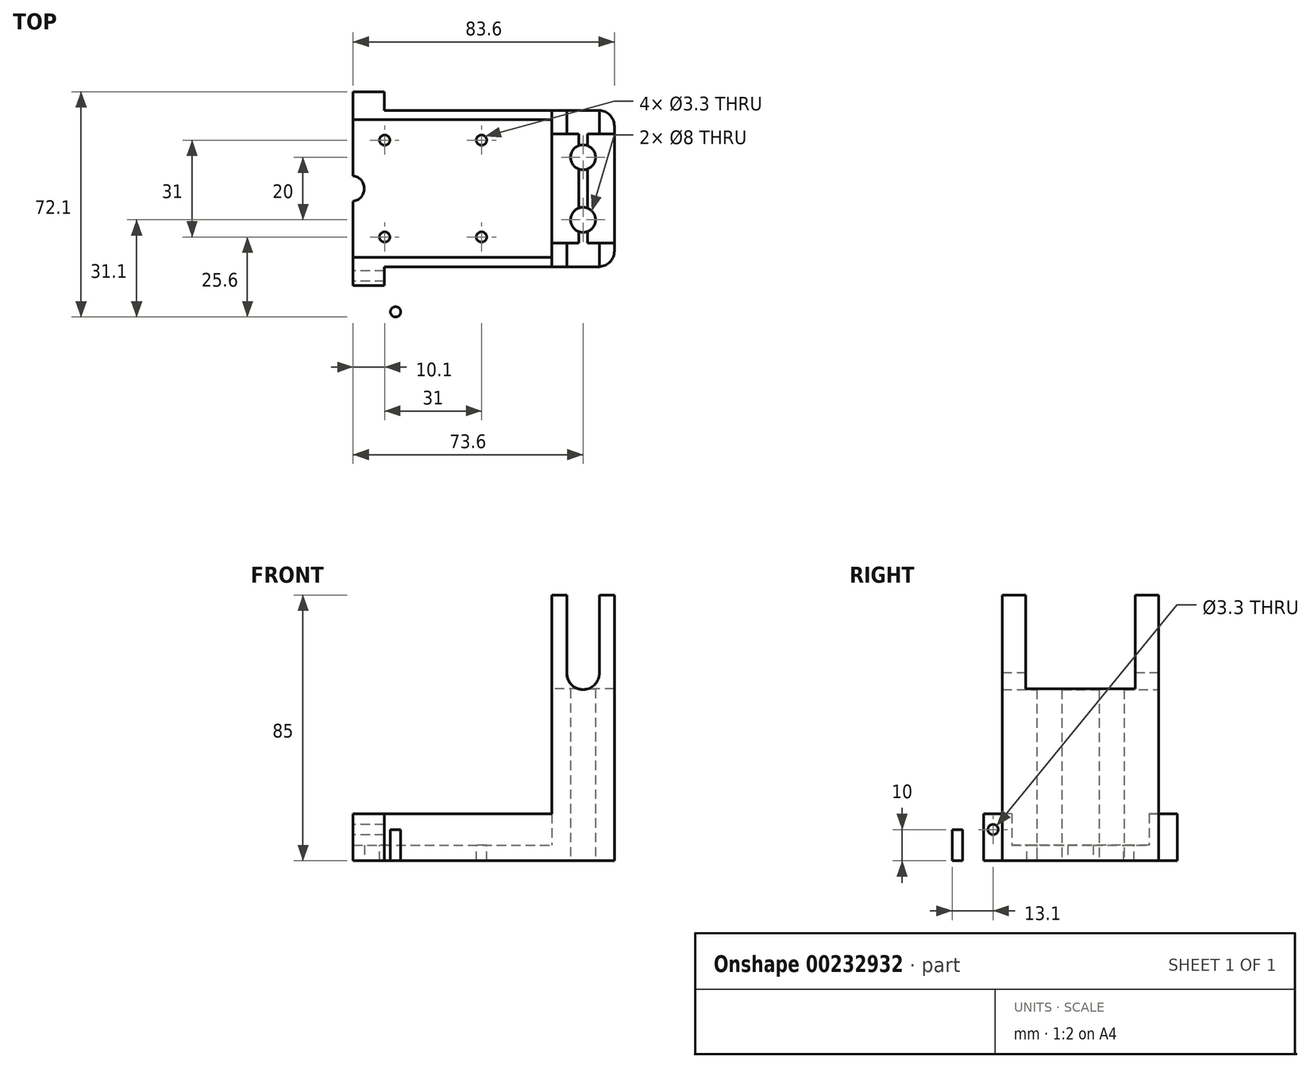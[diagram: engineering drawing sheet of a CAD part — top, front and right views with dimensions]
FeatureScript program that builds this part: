
annotation { "Feature Type Name" : "Feature", "Feature Type Description" : "" }
export const myFeature = defineFeature(function(context is Context, id is Id, definition is map)
    precondition{}
    {
        {
            var Q0;
            Q0=qCreatedBy(makeId("Top.planeOp"),FACE);
            var sketch = newSketch(context, id + "F0", { "sketchPlane" : qUnion([Q0])});
            skLineSegment(sketch, "E0.bottom", {"start": v(0, 0) * mm, "end": v(80, 0) * mm});
            skLineSegment(sketch, "E0.top", {"start": v(0, 50) * mm, "end": v(80, 50) * mm});
            skLineSegment(sketch, "E0.left", {"start": v(0, 0) * mm, "end": v(0, 50) * mm});
            skLineSegment(sketch, "E0.right", {"start": v(80, 0) * mm, "end": v(80, 50) * mm});
            skSolve(sketch);
        }
        {
            var Q0;
            Q0=makeQuery(id+"F0.imprint","IMPRINT",FACE,{"disambiguationData":[TD([[makeQuery(id+"F0.imprint","IMPRINT",EDGE,{"derivedFrom":sQuery(id+"F0.wireOp",EDGE,"E0.bottom")}),1.0]])]});
            extrude(context, id + "F1", {"entities" : qUnion([Q0]), "depth" : 5 * mm});
        }
        {
            var Q0;
            Q0=makeQuery(id+"F1.opExtrude","CAP_FACE",FACE,{"disambiguationData":[OSD([sQuery(id+"F0.wireOp",EDGE,"E0.bottom"),sQuery(id+"F0.wireOp",EDGE,"E0.top"),sQuery(id+"F0.wireOp",EDGE,"E0.left"),sQuery(id+"F0.wireOp",EDGE,"E0.right")])],"isStart":false});
            var sketch = newSketch(context, id + "F2", { "sketchPlane" : qUnion([Q0])});
            skLineSegment(sketch, "E1.0", {"start": v(3, 47) * mm, "end": v(77, 47) * mm});
            skLineSegment(sketch, "E1.2", {"start": v(3, 3) * mm, "end": v(77, 3) * mm});
            skLineSegment(sketch, "E1.3", {"start": v(77, 3) * mm, "end": v(77, 47) * mm});
            skPoint(sketch, "E2", {"position": v(60, 50) * mm});
            skLineSegment(sketch, "E3", {"start": v(60, 50) * mm, "end": v(60, 0) * mm});
            skLineSegment(sketch, "E4", {"start": v(3, 47) * mm, "end": v(0, 47) * mm});
            skLineSegment(sketch, "E5", {"start": v(3, 3) * mm, "end": v(0, 3) * mm});
            skPoint(sketch, "E6", {"position": v(6.5, 40.5) * mm});
            skPoint(sketch, "E7", {"position": v(6.5, 9.5) * mm});
            skPoint(sketch, "E8", {"position": v(37.5, 40.5) * mm});
            skPoint(sketch, "E9", {"position": v(37.5, 9.5) * mm});
            skSolve(sketch);
        }
        {
            var Q0;
            {var subQ5=sQuery(id+"F2.wireOp",EDGE,"E4");Q0=makeQuery(id+"F2.imprint","IMPRINT",FACE,{"disambiguationData":[TD([[makeQuery(id+"F2.imprint","IMPRINT",EDGE,{"derivedFrom":subQ5}),-1.0]])]});}
            var Q1;
            {var subQ5=sQuery(id+"F2.wireOp",EDGE,"E5");Q1=makeQuery(id+"F2.imprint","IMPRINT",FACE,{"disambiguationData":[TD([[makeQuery(id+"F2.imprint","IMPRINT",EDGE,{"derivedFrom":subQ5}),1.0]])]});}
            extrude(context, id + "F3", {"entities" : qUnion([Q0, Q1]), "operationType" : NewBodyOperationType.ADD, "depth" : 10 * mm});
        }
        {
            var Q0;
            {var subQ0=sQuery(id+"F2.wireOp",EDGE,"E1.3");Q0=makeQuery(id+"F2.imprint","IMPRINT",FACE,{"disambiguationData":[TD([[makeQuery(id+"F2.imprint","IMPRINT",EDGE,{"derivedFrom":subQ0}),1.0]])]});}
            var Q1;
            {var subQ0=sQuery(id+"F2.wireOp",EDGE,"E1.3");Q1=makeQuery(id+"F2.imprint","IMPRINT",FACE,{"disambiguationData":[TD([[makeQuery(id+"F2.imprint","IMPRINT",EDGE,{"derivedFrom":subQ0}),-1.0]])]});}
            extrude(context, id + "F4", {"entities" : qUnion([Q0, Q1]), "operationType" : NewBodyOperationType.ADD, "depth" : 80 * mm});
        }
        {
            var Q0;
            Q0=sQuery(id+"F2.wireOp",VERTEX,"E8");
            var Q1;
            Q1=sQuery(id+"F2.wireOp",VERTEX,"E9");
            var Q2;
            Q2=sQuery(id+"F2.wireOp",VERTEX,"E7");
            var Q3;
            Q3=sQuery(id+"F2.wireOp",VERTEX,"E6");
            var Q4;
            Q4=makeQuery(id+"F1.opExtrude","SWEPT_BODY",BODY,{"disambiguationData":[OSD([sQuery(id+"F0.wireOp",EDGE,"E0.bottom"),sQuery(id+"F0.wireOp",EDGE,"E0.top"),sQuery(id+"F0.wireOp",EDGE,"E0.left"),sQuery(id+"F0.wireOp",EDGE,"E0.right")])]});
            hole(context, id + "F5", {"style" : HoleStyle.SIMPLE, "endStyle" : HoleEndStyle.THROUGH, "standardTappedOrClearance" : lookupTablePath({ "standard" : "ISO", "fit" : "Normal", "size" : "M3", "type" : "Clearance" }), "standardBlindInLast" : lookupTablePath({ "fit" : "Standard", "standard" : "ISO", "size" : "M3", "type" : "Clearance" }), "holeDiameter" : 3.3 * mm, "tappedDepth" : 12 * mm, "tapClearance" : 3, "locations" : qUnion([Q0, Q1, Q2, Q3]), "scope" : qUnion([Q4])});
        }
        {
            var Q0;
            {var subQ0=sQuery(id+"F0.wireOp",EDGE,"E0.left");var subQ1=makeQuery(id+"F1.opExtrude","CAP_EDGE",EDGE,{"disambiguationData":[OSD([subQ0])],"isStart":false});Q0=makeQuery(id+"F3.boolean.opBoolean","MERGE",FACE,{"derivedFrom":[makeQuery(id+"F1.opExtrude","SWEPT_FACE",FACE,{"disambiguationData":[OSD([subQ0])]}),makeQuery(id+"F3.opExtrude","SWEPT_FACE",FACE,{"disambiguationData":[OSD([subQ0]),TDD([makeQuery(id+"F2.imprint","IMPRINT",EDGE,{"disambiguationData":[TD([[makeQuery(id+"F2.imprint","INTERSECT",VERTEX,{"derivedFrom":[makeQuery(id+"F1.opExtrude","CAP_EDGE",EDGE,{"disambiguationData":[OSD([sQuery(id+"F0.wireOp",EDGE,"E0.bottom")])],"isStart":false}),subQ1]}),-1.0]])],"derivedFrom":subQ1})])]}),makeQuery(id+"F3.opExtrude","SWEPT_FACE",FACE,{"disambiguationData":[OSD([subQ0]),TDD([makeQuery(id+"F2.imprint","IMPRINT",EDGE,{"disambiguationData":[TD([[makeQuery(id+"F2.imprint","INTERSECT",VERTEX,{"derivedFrom":[makeQuery(id+"F1.opExtrude","CAP_EDGE",EDGE,{"disambiguationData":[OSD([sQuery(id+"F0.wireOp",EDGE,"E0.top")])],"isStart":false}),subQ1]}),1.0]])],"derivedFrom":subQ1})])]})]});}
            extrude(context, id + "F6", {"entities" : qUnion([Q0]), "operationType" : NewBodyOperationType.ADD, "depth" : 3.6 * mm});
        }
        {
            var Q0;
            {var subQ0=sQuery(id+"F0.wireOp",EDGE,"E0.left");Q0=makeQuery(id+"F6.boolean.opBoolean","MERGE",FACE,{"derivedFrom":[makeQuery(id+"F1.opExtrude","CAP_FACE",FACE,{"disambiguationData":[OSD([sQuery(id+"F0.wireOp",EDGE,"E0.bottom"),sQuery(id+"F0.wireOp",EDGE,"E0.top"),subQ0,sQuery(id+"F0.wireOp",EDGE,"E0.right")])],"isStart":true}),makeQuery(id+"F6.opExtrude","SWEPT_FACE",FACE,{"disambiguationData":[OSD([subQ0]),TDD([makeQuery(id+"F1.opExtrude","CAP_EDGE",EDGE,{"disambiguationData":[OSD([subQ0])],"isStart":true})])]})]});}
            var sketch = newSketch(context, id + "F7", { "sketchPlane" : qUnion([Q0])});
            skPoint(sketch, "E10", {"position": v(-4.1, -25) * mm});
            skPoint(sketch, "E10.positionSnap0", {"position": v(-3.6, -25) * mm});
            skCircle(sketch, "E11", {"center": v(-4.1, -25) * mm, "radius": 4.1 * mm});
            skLineSegment(sketch, "E12", {"start": v(-4.1, -25) * mm, "end": v(-3.6, -25) * mm});
            skLineSegment(sketch, "E13", {"start": v(-3.6, -25) * mm, "end": v(-3.6, 0) * mm});
            skLineSegment(sketch, "E14", {"start": v(-3.6, -25) * mm, "end": v(-3.6, -50) * mm});
            skLineSegment(sketch, "E15.bottom", {"start": v(-3.6, -50) * mm, "end": v(6.4, -50) * mm});
            skLineSegment(sketch, "E15.top", {"start": v(-3.6, -56) * mm, "end": v(6.4, -56) * mm});
            skLineSegment(sketch, "E15.left", {"start": v(-3.6, -50) * mm, "end": v(-3.6, -56) * mm});
            skLineSegment(sketch, "E15.right", {"start": v(6.4, -50) * mm, "end": v(6.4, -56) * mm});
            skLineSegment(sketch, "E16", {"start": v(-3.6, -25) * mm, "end": v(10.88, -25) * mm, "construction": true});
            skLineSegment(sketch, "E17.MirrorCS", {"start": v(-3.6, 6) * mm, "end": v(6.4, 6) * mm});
            skLineSegment(sketch, "E18.MirrorCS", {"start": v(6.4, 0) * mm, "end": v(6.4, 6) * mm});
            skLineSegment(sketch, "E19.MirrorCS", {"start": v(-3.6, 0) * mm, "end": v(-3.6, 6) * mm});
            skSolve(sketch);
        }
        {
            var Q0;
            {var subQ0=sQuery(id+"F7.wireOp",EDGE,"E13");var subQ1=sQuery(id+"F7.wireOp",EDGE,"E11");var subQ2=makeQuery(id+"F7.imprint","INTERSECT",VERTEX,{"derivedFrom":[subQ1,subQ0]});Q0=makeQuery(id+"F7.imprint","IMPRINT",FACE,{"disambiguationData":[TD([[makeQuery(id+"F7.imprint","IMPRINT",EDGE,{"disambiguationData":[TD([[subQ2,1.0]])],"derivedFrom":subQ1}),1.0]])]});}
            extrude(context, id + "F8", {"entities" : qUnion([Q0]), "operationType" : NewBodyOperationType.REMOVE, "oppositeDirection" : true, "depth" : 25 * mm});
        }
        {
            var Q0;
            Q0=makeQuery(id+"F7.imprint","IMPRINT",FACE,{"disambiguationData":[TD([[makeQuery(id+"F7.imprint","IMPRINT",EDGE,{"derivedFrom":sQuery(id+"F7.wireOp",EDGE,"E17.MirrorCS")}),-1.0]])]});
            var Q1;
            Q1=makeQuery(id+"F7.imprint","IMPRINT",FACE,{"disambiguationData":[TD([[makeQuery(id+"F7.imprint","IMPRINT",EDGE,{"derivedFrom":sQuery(id+"F7.wireOp",EDGE,"E15.bottom")}),-1.0]])]});
            extrude(context, id + "F9", {"entities" : qUnion([Q0, Q1]), "operationType" : NewBodyOperationType.ADD, "oppositeDirection" : true, "depth" : 15 * mm});
        }
        {
            var Q0;
            {var subQ0=sQuery(id+"F0.wireOp",EDGE,"E0.left");var subQ1=sQuery(id+"F0.wireOp",EDGE,"E0.bottom");Q0=makeQuery(id+"F9.boolean.opBoolean","MERGE",FACE,{"derivedFrom":[makeQuery(id+"F8.boolean.opBoolean","SPLIT",FACE,{"disambiguationData":[TD([makeQuery(id+"F1.opExtrude","SWEPT_FACE",FACE,{"disambiguationData":[OSD([subQ1])]})])],"derivedFrom":makeQuery(id+"F6.opExtrude","CAP_FACE",FACE,{"disambiguationData":[OSD([subQ0])],"isStart":false})}),makeQuery(id+"F9.opExtrude","SWEPT_FACE",FACE,{"disambiguationData":[OSD([sQuery(id+"F7.wireOp",EDGE,"E19.MirrorCS")])]})]});}
            var sketch = newSketch(context, id + "F10", { "sketchPlane" : qUnion([Q0])});
            skCircle(sketch, "E20", {"center": v(3, 10) * mm, "radius": 1.65 * mm});
            skPoint(sketch, "E20.centerSnap0", {"position": v(-3, 10) * mm});
            skPoint(sketch, "E21.0", {"position": v(-25, 0) * mm});
            skLineSegment(sketch, "E22", {"start": v(-25, 0) * mm, "end": v(-25, 12.79) * mm, "construction": true});
            skCircle(sketch, "E23.MirrorC", {"center": v(-53, 10) * mm, "radius": 1.65 * mm});
            skSolve(sketch);
        }
        {
            var Q0;
            Q0=makeQuery(id+"F10.imprint","IMPRINT",FACE,{"disambiguationData":[TD([[makeQuery(id+"F10.imprint","IMPRINT",EDGE,{"derivedFrom":sQuery(id+"F10.wireOp",EDGE,"E20")}),1.0]])]});
            var Q1;
            Q1=makeQuery(id+"F10.imprint","IMPRINT",FACE,{"disambiguationData":[TD([[makeQuery(id+"F10.imprint","IMPRINT",EDGE,{"derivedFrom":sQuery(id+"F10.wireOp",EDGE,"E23.MirrorC")}),-1.0]])]});
            extrude(context, id + "F11", {"entities" : qUnion([Q0, Q1]), "operationType" : NewBodyOperationType.REMOVE, "oppositeDirection" : true, "depth" : 25 * mm});
        }
        {
            var Q0;
            Q0=qCreatedBy(makeId("Top.planeOp"),FACE);
            var sketch = newSketch(context, id + "F12", { "sketchPlane" : qUnion([Q0])});
            skLineSegment(sketch, "E24.bottom", {"start": v(0, -11.45) * mm, "end": v(15, -11.45) * mm});
            skLineSegment(sketch, "E24.top", {"start": v(0, -73.45) * mm, "end": v(15, -73.45) * mm});
            skLineSegment(sketch, "E24.left", {"start": v(0, -11.45) * mm, "end": v(0, -73.45) * mm});
            skLineSegment(sketch, "E24.right", {"start": v(15, -11.45) * mm, "end": v(15, -73.45) * mm});
            skPoint(sketch, "E25", {"position": v(15, -20.45) * mm});
            skPoint(sketch, "E26", {"position": v(5, -20.45) * mm});
            skLineSegment(sketch, "E27", {"start": v(0, -42.45) * mm, "end": v(8.49, -42.45) * mm, "construction": true});
            skPoint(sketch, "E27.endSnap0", {"position": v(0, -42.45) * mm});
            skLineSegment(sketch, "E28", {"start": v(5, -20.45) * mm, "end": v(15, -20.45) * mm});
            skLineSegment(sketch, "E29", {"start": v(5, -20.45) * mm, "end": v(5, -42.45) * mm});
            skLineSegment(sketch, "E30.MirrorCS", {"start": v(5, -64.45) * mm, "end": v(5, -42.45) * mm});
            skLineSegment(sketch, "E31.MirrorCS", {"start": v(5, -64.45) * mm, "end": v(15, -64.45) * mm});
            skSolve(sketch);
        }
        {
            var Q0;
            {var subQ1=sQuery(id+"F12.wireOp",EDGE,"E24.bottom");Q0=makeQuery(id+"F12.imprint","IMPRINT",FACE,{"disambiguationData":[TD([[makeQuery(id+"F12.imprint","IMPRINT",EDGE,{"derivedFrom":subQ1}),-1.0]])]});}
            extrude(context, id + "F13", {"entities" : qUnion([Q0]), "depth" : 10 * mm});
        }
        {
            var Q0;
            Q0=makeQuery(id+"F13.opExtrude","SWEPT_FACE",FACE,{"disambiguationData":[OSD([sQuery(id+"F12.wireOp",EDGE,"E29"),sQuery(id+"F12.wireOp",EDGE,"E30.MirrorCS")])]});
            var sketch = newSketch(context, id + "F14", { "sketchPlane" : qUnion([Q0])});
            skPoint(sketch, "E32", {"position": v(-42.45, -0.5) * mm});
            skPoint(sketch, "E32.positionSnap0", {"position": v(-42.45, 0) * mm});
            skCircle(sketch, "E33", {"center": v(-42.45, -0.5) * mm, "radius": 4.1 * mm});
            skSolve(sketch);
        }
        {
            var Q0;
            {var subQ0=sQuery(id+"F14.wireOp",EDGE,"E33");var subQ1=makeQuery(id+"F13.opExtrude","CAP_EDGE",EDGE,{"disambiguationData":[OSD([sQuery(id+"F12.wireOp",EDGE,"E29"),sQuery(id+"F12.wireOp",EDGE,"E30.MirrorCS")])],"isStart":true});var subQ2=makeQuery(id+"F14.imprint","INTERSECT",VERTEX,{"disambiguationData":[OD(0.0)],"derivedFrom":[subQ1,subQ0]});Q0=makeQuery(id+"F14.imprint","IMPRINT",FACE,{"disambiguationData":[TD([[makeQuery(id+"F14.imprint","IMPRINT",EDGE,{"disambiguationData":[TD([[subQ2,-1.0]])],"derivedFrom":subQ0}),1.0]])]});}
            extrude(context, id + "F15", {"entities" : qUnion([Q0]), "operationType" : NewBodyOperationType.REMOVE, "oppositeDirection" : true, "depth" : 25 * mm});
        }
        {
            var Q0;
            Q0=makeQuery(id+"F13.opExtrude","CAP_FACE",FACE,{"disambiguationData":[OSD([sQuery(id+"F12.wireOp",EDGE,"E24.bottom"),sQuery(id+"F12.wireOp",EDGE,"E24.top"),sQuery(id+"F12.wireOp",EDGE,"E24.left"),sQuery(id+"F12.wireOp",EDGE,"E24.right"),sQuery(id+"F12.wireOp",EDGE,"E28"),sQuery(id+"F12.wireOp",EDGE,"E29"),sQuery(id+"F12.wireOp",EDGE,"E30.MirrorCS"),sQuery(id+"F12.wireOp",EDGE,"E31.MirrorCS")])],"isStart":false});
            var sketch = newSketch(context, id + "F16", { "sketchPlane" : qUnion([Q0])});
            skPoint(sketch, "E34", {"position": v(10, -70.45) * mm});
            skLineSegment(sketch, "E35", {"start": v(5, -42.45) * mm, "end": v(11.3, -42.45) * mm, "construction": true});
            skCircle(sketch, "E36", {"center": v(10, -70.45) * mm, "radius": 1.65 * mm});
            skCircle(sketch, "E37.MirrorC", {"center": v(10, -14.45) * mm, "radius": 1.65 * mm});
            skSolve(sketch);
        }
        {
            var Q0;
            Q0=makeQuery(id+"F16.imprint","IMPRINT",FACE,{"disambiguationData":[TD([[makeQuery(id+"F16.imprint","IMPRINT",EDGE,{"derivedFrom":sQuery(id+"F16.wireOp",EDGE,"E37.MirrorC")}),-1.0]])]});
            var Q1;
            Q1=makeQuery(id+"F16.imprint","IMPRINT",FACE,{"disambiguationData":[TD([[makeQuery(id+"F16.imprint","IMPRINT",EDGE,{"derivedFrom":sQuery(id+"F16.wireOp",EDGE,"E36")}),1.0]])]});
            extrude(context, id + "F17", {"entities" : qUnion([Q0, Q1]), "operationType" : NewBodyOperationType.REMOVE, "oppositeDirection" : true, "depth" : 25 * mm});
        }
        {
            var Q0;
            {var subQ0=sQuery(id+"F0.wireOp",EDGE,"E0.top");Q0=makeQuery(id+"F6.boolean.opBoolean","MERGE",FACE,{"derivedFrom":[makeQuery(id+"F4.boolean.opBoolean","MERGE",FACE,{"derivedFrom":[makeQuery(id+"F3.boolean.opBoolean","MERGE",FACE,{"derivedFrom":[makeQuery(id+"F1.opExtrude","SWEPT_FACE",FACE,{"disambiguationData":[OSD([subQ0])]}),makeQuery(id+"F3.opExtrude","SWEPT_FACE",FACE,{"disambiguationData":[OSD([subQ0])]})]}),makeQuery(id+"F4.opExtrude","SWEPT_FACE",FACE,{"disambiguationData":[OSD([subQ0])]})]}),makeQuery(id+"F6.opExtrude","SWEPT_FACE",FACE,{"disambiguationData":[OSD([subQ0,sQuery(id+"F0.wireOp",EDGE,"E0.left")])]})]});}
            var sketch = newSketch(context, id + "F18", { "sketchPlane" : qUnion([Q0])});
            skPoint(sketch, "E38", {"position": v(-70, 60) * mm});
            skPoint(sketch, "E38.positionSnap0", {"position": v(-70, 85) * mm});
            skCircle(sketch, "E39", {"center": v(-70, 60) * mm, "radius": 5.2 * mm});
            skLineSegment(sketch, "E40", {"start": v(-75.2, 60.25) * mm, "end": v(-75.2, 85) * mm});
            skLineSegment(sketch, "E41", {"start": v(-64.8, 60) * mm, "end": v(-64.8, 85) * mm});
            skSolve(sketch);
        }
        {
            var Q0;
            Q0=makeQuery(id+"F4.opExtrude","CAP_FACE",FACE,{"disambiguationData":[OSD([sQuery(id+"F0.wireOp",EDGE,"E0.bottom"),sQuery(id+"F0.wireOp",EDGE,"E0.top"),sQuery(id+"F0.wireOp",EDGE,"E0.right"),sQuery(id+"F2.wireOp",EDGE,"E3")])],"isStart":false});
            var sketch = newSketch(context, id + "F19", { "sketchPlane" : qUnion([Q0])});
            skPoint(sketch, "E42", {"position": v(80, 25) * mm});
            skPoint(sketch, "E43", {"position": v(80, 42.5) * mm});
            skPoint(sketch, "E44", {"position": v(80, 7.5) * mm});
            skLineSegment(sketch, "E45", {"start": v(80, 7.5) * mm, "end": v(60, 7.5) * mm});
            skLineSegment(sketch, "E46", {"start": v(80, 42.5) * mm, "end": v(60, 42.5) * mm});
            skSolve(sketch);
        }
        {
            var Q0;
            {var subQ0=sQuery(id+"F19.wireOp",EDGE,"E45");Q0=makeQuery(id+"F19.imprint","IMPRINT",FACE,{"disambiguationData":[TD([[makeQuery(id+"F19.imprint","IMPRINT",EDGE,{"derivedFrom":subQ0}),-1.0]])]});}
            extrude(context, id + "F20", {"entities" : qUnion([Q0]), "operationType" : NewBodyOperationType.REMOVE, "oppositeDirection" : true, "depth" : 30 * mm});
        }
        {
            var Q0;
            Q0 = qSketchRegion(id + "F18", true);
            var Q1;
            {var subQ0=sQuery(id+"F18.wireOp",EDGE,"E40");Q1=makeQuery(id+"F18.imprint","IMPRINT",FACE,{"disambiguationData":[TD([[makeQuery(id+"F18.imprint","IMPRINT",EDGE,{"derivedFrom":subQ0}),-1.0]])]});}
            extrude(context, id + "F21", {"entities" : qUnion([Q0, Q1]), "operationType" : NewBodyOperationType.REMOVE, "oppositeDirection" : true, "depth" : 80 * mm});
        }
        {
            var Q0;
            {var subQ5=sQuery(id+"F7.wireOp",EDGE,"E15.bottom");Q0=makeQuery(id+"F7.imprint","IMPRINT",FACE,{"disambiguationData":[TD([[makeQuery(id+"F7.imprint","IMPRINT",EDGE,{"derivedFrom":subQ5}),1.0]])]});}
            var sketch = newSketch(context, id + "F22", { "sketchPlane" : qUnion([Q0])});
            skPoint(sketch, "E47.0", {"position": v(80, 0) * mm});
            skPoint(sketch, "E48", {"position": v(70, 0) * mm});
            skPoint(sketch, "E49.0", {"position": v(80, -25) * mm});
            skPoint(sketch, "E50", {"position": v(70, -25) * mm});
            skCircle(sketch, "E51", {"center": v(70, -15) * mm, "radius": 4 * mm});
            skCircle(sketch, "E52", {"center": v(70, -35) * mm, "radius": 4 * mm});
            skSolve(sketch);
        }
        {
            var Q0;
            Q0=makeQuery(id+"F22.imprint","IMPRINT",FACE,{"disambiguationData":[TD([[makeQuery(id+"F22.imprint","IMPRINT",EDGE,{"derivedFrom":sQuery(id+"F22.wireOp",EDGE,"E51")}),1.0]])]});
            var Q1;
            Q1=makeQuery(id+"F22.imprint","IMPRINT",FACE,{"disambiguationData":[TD([[makeQuery(id+"F22.imprint","IMPRINT",EDGE,{"derivedFrom":sQuery(id+"F22.wireOp",EDGE,"E52")}),1.0]])]});
            extrude(context, id + "F23", {"entities" : qUnion([Q0, Q1]), "operationType" : NewBodyOperationType.REMOVE, "oppositeDirection" : true, "depth" : 60 * mm});
        }
        {
            var Q0;
            {var subQ0=sQuery(id+"F0.wireOp",EDGE,"E0.right");var subQ1=sQuery(id+"F0.wireOp",EDGE,"E0.top");Q0=makeQuery(id+"F4.boolean.opBoolean","MERGE",EDGE,{"derivedFrom":[makeQuery(id+"F1.opExtrude","SWEPT_EDGE",EDGE,{"disambiguationData":[OSD([subQ1,subQ0])]}),makeQuery(id+"F4.opExtrude","SWEPT_EDGE",EDGE,{"disambiguationData":[OSD([subQ1,subQ0])]})]});}
            var Q1;
            {var subQ0=sQuery(id+"F0.wireOp",EDGE,"E0.right");var subQ1=sQuery(id+"F0.wireOp",EDGE,"E0.bottom");Q1=makeQuery(id+"F4.boolean.opBoolean","MERGE",EDGE,{"derivedFrom":[makeQuery(id+"F1.opExtrude","SWEPT_EDGE",EDGE,{"disambiguationData":[OSD([subQ1,subQ0])]}),makeQuery(id+"F4.opExtrude","SWEPT_EDGE",EDGE,{"disambiguationData":[OSD([subQ1,subQ0])]})]});}
            var Q2;
            Q2=makeQuery(id+"F3.opExtrude","SWEPT_EDGE",EDGE,{"disambiguationData":[OSD([sQuery(id+"F2.wireOp",EDGE,"E1.0"),sQuery(id+"F2.wireOp",EDGE,"E3")])]});
            var Q3;
            Q3=makeQuery(id+"F3.opExtrude","SWEPT_EDGE",EDGE,{"disambiguationData":[OSD([sQuery(id+"F2.wireOp",EDGE,"E1.2"),sQuery(id+"F2.wireOp",EDGE,"E3")])]});
            var Q4;
            {var subQ0=sQuery(id+"F2.wireOp",EDGE,"E3");Q4=makeQuery(id+"F3.opExtrude","CAP_EDGE",EDGE,{"disambiguationData":[OSD([subQ0]),TDD([makeQuery(id+"F2.imprint","IMPRINT",EDGE,{"disambiguationData":[TD([[makeQuery(id+"F2.imprint","INTERSECT",VERTEX,{"derivedFrom":[makeQuery(id+"F1.opExtrude","CAP_EDGE",EDGE,{"disambiguationData":[OSD([sQuery(id+"F0.wireOp",EDGE,"E0.bottom")])],"isStart":false}),subQ0]}),1.0]])],"derivedFrom":subQ0})])],"isStart":false});}
            var Q5;
            {var subQ0=sQuery(id+"F2.wireOp",EDGE,"E3");Q5=makeQuery(id+"F3.opExtrude","CAP_EDGE",EDGE,{"disambiguationData":[OSD([subQ0]),TDD([makeQuery(id+"F2.imprint","IMPRINT",EDGE,{"disambiguationData":[TD([[makeQuery(id+"F2.imprint","INTERSECT",VERTEX,{"derivedFrom":[makeQuery(id+"F1.opExtrude","CAP_EDGE",EDGE,{"disambiguationData":[OSD([sQuery(id+"F0.wireOp",EDGE,"E0.top")])],"isStart":false}),subQ0]}),-1.0]])],"derivedFrom":subQ0})])],"isStart":false});}
            fillet(context, id + "F24", {"entities" : qUnion([Q0, Q1, Q2, Q3, Q4, Q5]), "radius" : 5 * mm, "tangentPropagation" : true, "allowEdgeOverflow" : false});
        }
    });
